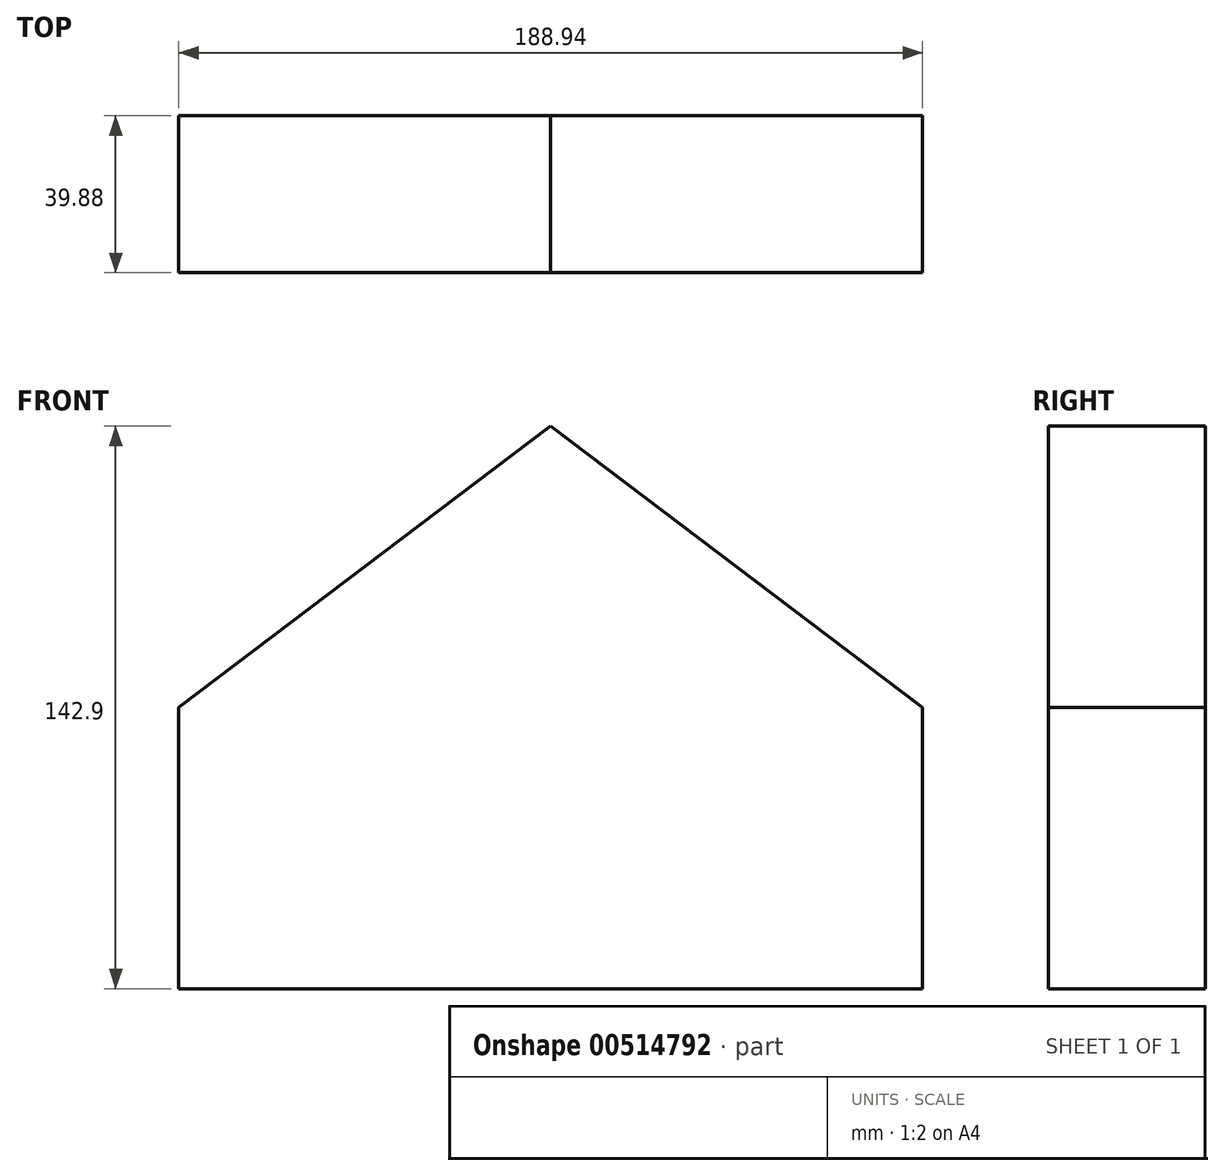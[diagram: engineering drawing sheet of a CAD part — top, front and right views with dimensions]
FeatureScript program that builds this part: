
annotation { "Feature Type Name" : "Feature", "Feature Type Description" : "" }
export const myFeature = defineFeature(function(context is Context, id is Id, definition is map)
    precondition{}
    {
        {
            var Q0;
            Q0=qCreatedBy(makeId("Front.planeOp"),FACE);
            var sketch = newSketch(context, id + "F0", { "sketchPlane" : qUnion([Q0])});
            skLineSegment(sketch, "E0.top", {"start": v(-71.13, -83.2) * mm, "end": v(117.8, -83.2) * mm});
            skLineSegment(sketch, "E1", {"start": v(-71.13, -11.75) * mm, "end": v(23.34, 59.7) * mm});
            skLineSegment(sketch, "E2", {"start": v(23.34, 59.7) * mm, "end": v(117.8, -11.75) * mm});
            skLineSegment(sketch, "E3", {"start": v(-71.13, -11.75) * mm, "end": v(-71.13, -83.2) * mm});
            skLineSegment(sketch, "E4", {"start": v(117.8, -11.75) * mm, "end": v(117.8, -83.2) * mm});
            skSolve(sketch);
        }
        {
            var Q0;
            Q0 = qSketchRegion(id + "F0", true);
            extrude(context, id + "F1", {"entities" : qUnion([Q0]), "depth" : 39.88 * mm, "offsetDistance" : 25.4 * mm});
        }
    });
